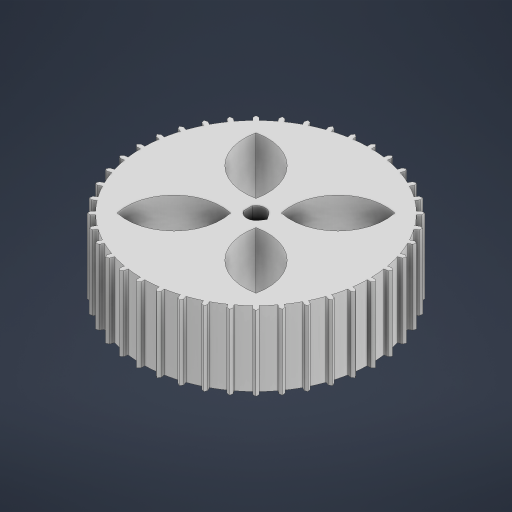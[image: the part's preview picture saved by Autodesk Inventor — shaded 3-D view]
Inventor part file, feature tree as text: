
AUTODESK INVENTOR PART (.ipt)
format: ipt  version: 2024.2 (Build 282272000, 272)  size: 989,696 bytes
history: native  units: in
note: dims shown in document units (in); Inventor stores cm internally (conversion verified against a paired STEP export)
features: chamfer x10, extrude x4, sketch x4, pattern_circular x2, plane x1
ambient origin geometry x8: Origin, YZ Plane, XZ Plane, XY Plane, X Axis, Y Axis, Z Axis, Center Point
bodies: Solid1 (feature_tree)
feature tree (21):
  extrude  "Extrusion1"  Depth=0.2441in
  plane  "Work Plane1"
  extrude  "Extrusion4"  Depth=0.9843in TaperAngle=45.0deg
  pattern_circular  "Circular Pattern4"  Angle=45.0deg  [1 undecoded]
  extrude  "Extrusion5"  Depth=0.0787in TaperAngle=45.0deg
  extrude  "Extrusion6"  Depth=0.0787in TaperAngle=45.0deg
  chamfer  "Chamfer8"  Distance=0.1in Angle=45.0deg
  chamfer  "Chamfer9"  Distance=0.1in Angle=45.0deg
  chamfer  "Chamfer10"  Distance=0.1in Angle=45.0deg
  chamfer  "Chamfer11"  Distance=0.1in Angle=45.0deg
  chamfer  "Chamfer12"  Distance=9.4488in Angle=360.0deg
  chamfer  "Chamfer13"  Distance=0.0625in
  chamfer  "Chamfer14"  Distance=0.1476in
  chamfer  "Chamfer15"  Distance=0.1083in
  chamfer  "Chamfer16"  Distance=0.0787in
  chamfer  "Chamfer17"  Distance=0.0295in
  pattern_circular  "Circular Pattern2"  [2 undecoded]
  sketch  "Sketch1"  dims[d0=3.0in d1=0.2441in]
  sketch  "Sketch4"  dims[d3=0.9843in d4=0.0in d63=0.1in d64=0.075in d65=45.0deg]
  sketch  "Sketch5"  dims[d66=0.1in d67=0.075in d68=45.0deg]
  sketch  "Sketch6"  dims[d69=0.1in d70=0.075in d71=45.0deg d72=0.1in d73=0.075in d74=45.0deg d75=0.1in d76=0.075in d77=45.0deg d78=0.1in d79=0.075in d80=45.0deg d81=0.1in d82=0.075in d83=45.0deg d84=0.1in d85=0.075in d86=45.0deg d87=0.1in d88=0.075in d89=45.0deg d90=0.1in d91=0.075in d92=45.0deg d93=9.4488in d94=360.0deg d96=0.0625in d116=0.1476in d117=0.1083in d118=0.0787in d119=0.0295in d120=0.0295in d121=0.0295in d122=0.0295in d123=0.0295in d124=0.9843in d125=0.0in d126=15.748in d127=360.0deg d129=0.4724in d131=135.0deg d132=0.6299in d133=0.0in d134=0.0in d135=0.0787in d136=0.0in d105=0.0in d106=0.0in d107=0.0in d108=0.0in]
note: 3 required parameter values undecoded (feature->parameter linkage not recoverable at this tier; creation-order binding heuristic only, values carry confidence <= 0.55)
